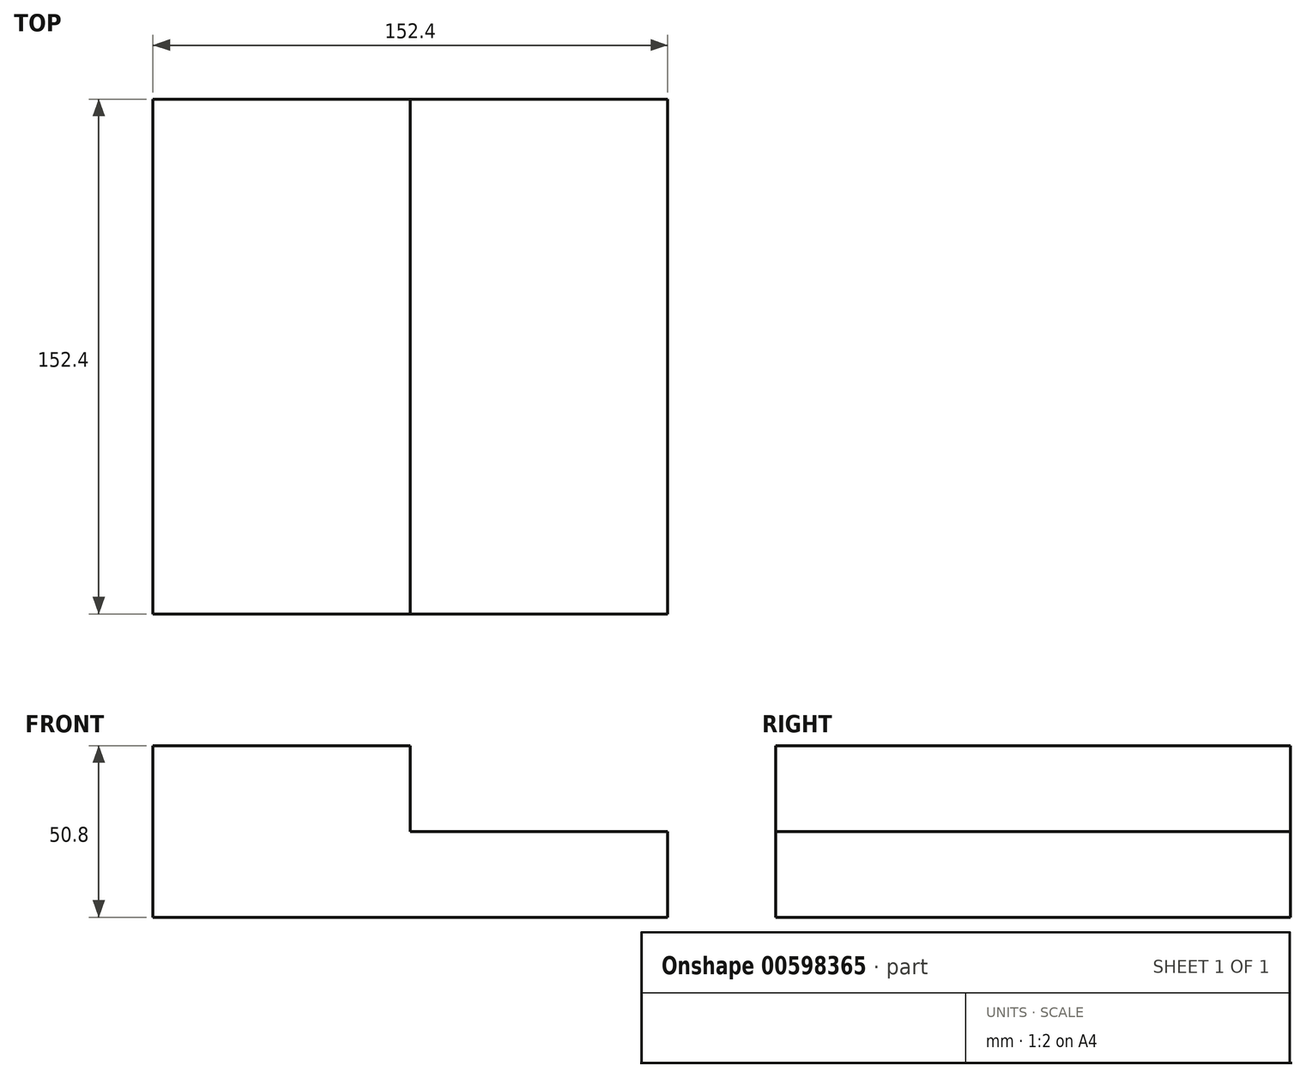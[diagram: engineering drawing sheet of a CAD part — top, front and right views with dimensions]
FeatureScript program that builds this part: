
annotation { "Feature Type Name" : "Feature", "Feature Type Description" : "" }
export const myFeature = defineFeature(function(context is Context, id is Id, definition is map)
    precondition{}
    {
        {
            var Q0;
            Q0=qCreatedBy(makeId("Front.planeOp"),FACE);
            var sketch = newSketch(context, id + "F0", { "sketchPlane" : qUnion([Q0])});
            skLineSegment(sketch, "E0", {"start": v(-75.44, 0) * mm, "end": v(76.96, 0) * mm});
            skLineSegment(sketch, "E1", {"start": v(-75.44, 0) * mm, "end": v(-75.44, 50.8) * mm});
            skLineSegment(sketch, "E2", {"start": v(-75.44, 50.8) * mm, "end": v(0.76, 50.8) * mm});
            skLineSegment(sketch, "E3", {"start": v(0.76, 50.8) * mm, "end": v(0.76, 25.4) * mm});
            skLineSegment(sketch, "E4", {"start": v(0.76, 25.4) * mm, "end": v(78.55, 25.4) * mm});
            skLineSegment(sketch, "E5", {"start": v(76.96, 0) * mm, "end": v(76.96, 25.4) * mm});
            skSolve(sketch);
        }
        {
            var Q0;
            Q0=makeQuery(id+"F0.imprint","IMPRINT",FACE,{"disambiguationData":[TD([[makeQuery(id+"F0.imprint","IMPRINT",EDGE,{"derivedFrom":sQuery(id+"F0.wireOp",EDGE,"E0")}),1.0]])]});
            extrude(context, id + "F1", {"entities" : qUnion([Q0]), "depth" : 152.4 * mm, "offsetDistance" : 25.4 * mm});
        }
    });
